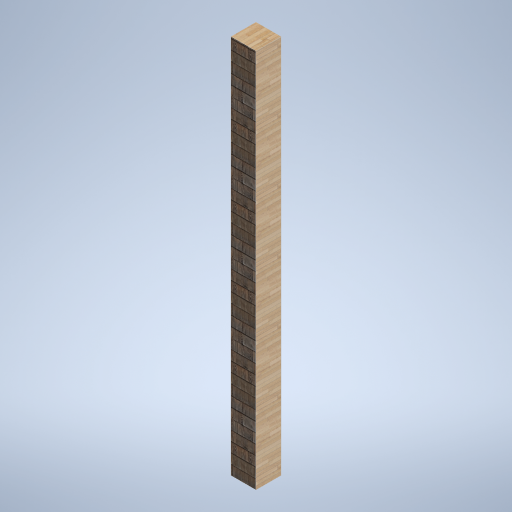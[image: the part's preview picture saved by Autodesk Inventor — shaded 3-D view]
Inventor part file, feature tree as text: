
AUTODESK INVENTOR PART (.ipt)
format: ipt  version: 2024.2 (Build 282272000, 272)  size: 308,736 bytes
history: native  units: in
note: dims shown in document units (in); Inventor stores cm internally (conversion verified against a paired STEP export)
features: other x3, sketch x1
ambient origin geometry x8: Origin, YZ Plane, XZ Plane, XY Plane, X Axis, Y Axis, Z Axis, Center Point
bodies: Solid1 (feature_tree)
feature tree (4):
  other  "support_frame_03.ipt"
  other  "Solid1::support_frame_03.ipt"
  other  "TaggingFeature1"
  sketch  "Sketch1"  dims[d0=0.3937in]
